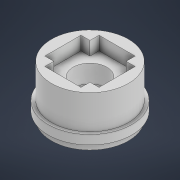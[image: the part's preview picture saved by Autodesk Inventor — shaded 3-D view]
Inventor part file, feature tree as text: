
AUTODESK INVENTOR PART (.ipt)
format: ipt  version: 2021 (Build 250183000, 183)  size: 221,696 bytes
history: native  units: mm (DEFAULTED — no unit token found)
features: extrude x9, sketch x9, plane x1
ambient origin geometry x8: Origin, YZ Plane, XZ Plane, XY Plane, X Axis, Y Axis, Z Axis, Center Point
bodies: Volumenkörper1 (feature_tree)
feature tree (19):
  extrude  "Extrusion1"  Depth=12.0mm
  extrude  "Extrusion3"  Depth=6.0mm TaperAngle=0.0deg
  extrude  "Extrusion9"  Depth=12.0mm
  extrude  "Extrusion10"  Depth=12.0mm TaperAngle=0.0deg
  extrude  "Extrusion12"  Depth=4.0mm TaperAngle=0.0deg
  extrude  "Extrusion13"  Depth=2.0mm
  extrude  "Extrusion14"  Depth=2.0mm
  extrude  "Extrusion15"  Depth=2.0mm
  plane  "Arbeitsebene2"
  extrude  "Extrusion16"  Depth=2.0mm
  sketch  "Skizze1"  dims[d10=12.0mm d12=17.0mm]
  sketch  "Skizze3"  dims[d21=6.0mm d22=0.0mm d33=6.0mm d34=0.0mm]
  sketch  "Skizze9"  dims[d53=12.0mm d54=12.0mm]
  sketch  "Skizze10"  dims[d55=12.0mm d56=6.0mm d57=0.0mm]
  sketch  "Skizze12"  dims[d58=7.5mm d59=4.0mm d60=0.0mm]
  sketch  "Skizze13"  dims[d64=2.0mm d65=2.0mm]
  sketch  "Skizze14"  dims[d66=2.0mm d67=2.0mm]
  sketch  "Skizze15"  dims[d68=2.0mm d69=2.0mm]
  sketch  "Skizze17"  dims[d70=2.0mm d71=2.0mm d72=4.0mm d73=0.0mm d76=3.0mm d77=3.0mm d78=3.0mm d79=3.0mm d80=3.0mm d81=3.0mm d82=3.0mm d83=3.0mm d84=90.0deg d85=2.5mm d86=2.5mm d87=2.5mm d88=2.5mm d89=90.0deg d90=17.0mm d91=2.0mm d92=0.0mm d93=3.2mm d94=2.0mm d95=0.0mm d96=18.0mm d97=3.0mm d98=0.0mm d99=17.0mm d101=-1.5mm d102=18.5mm d103=2.0mm d104=0.0mm]
